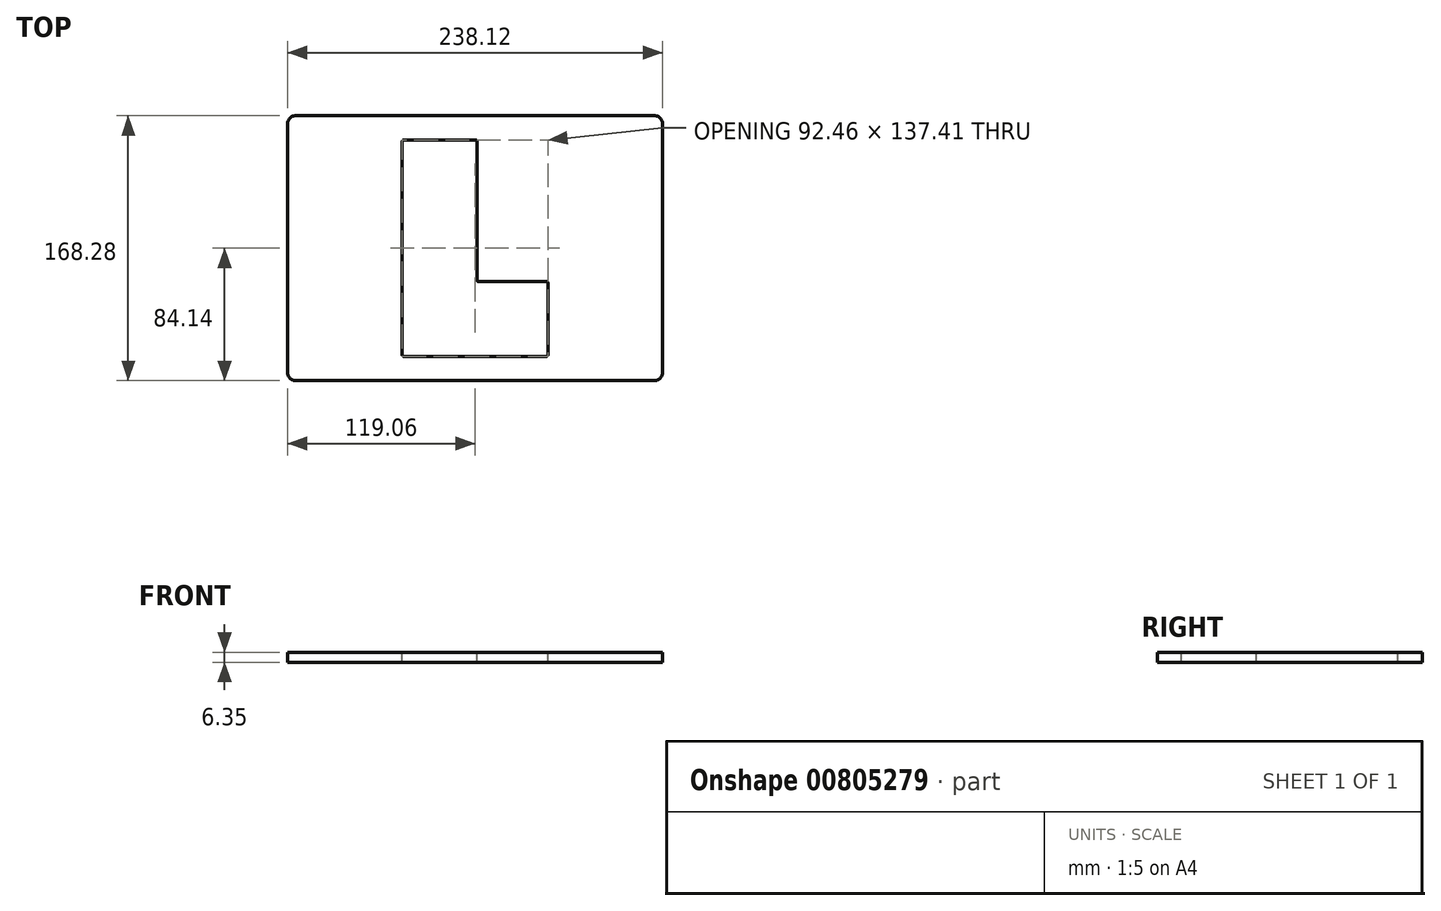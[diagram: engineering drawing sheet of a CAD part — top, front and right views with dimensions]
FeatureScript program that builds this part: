
annotation { "Feature Type Name" : "Feature", "Feature Type Description" : "" }
export const myFeature = defineFeature(function(context is Context, id is Id, definition is map)
    precondition{}
    {
        {
            var Q0;
            Q0=qCreatedBy(makeId("Top.planeOp"),FACE);
            var sketch = newSketch(context, id + "F0", { "sketchPlane" : qUnion([Q0])});
            skLineSegment(sketch, "E0.bottom", {"start": v(-119.06, 84.14) * mm, "end": v(119.06, 84.14) * mm});
            skLineSegment(sketch, "E0.top", {"start": v(-119.06, -84.14) * mm, "end": v(119.06, -84.14) * mm});
            skLineSegment(sketch, "E0.left", {"start": v(-119.06, 84.14) * mm, "end": v(-119.06, -84.14) * mm});
            skLineSegment(sketch, "E0.right", {"start": v(119.06, 84.14) * mm, "end": v(119.06, -84.14) * mm});
            skPoint(sketch, "E0.middle", {"position": v(0, 0) * mm});
            skSolve(sketch);
        }
        {
            var Q0;
            Q0 = qSketchRegion(id + "F0", true);
            extrude(context, id + "F1", {"entities" : qUnion([Q0]), "depth" : 6.35 * mm, "offsetDistance" : 25.4 * mm});
        }
        {
            var Q0;
            Q0=makeQuery(id+"F1.opExtrude","CAP_FACE",FACE,{"disambiguationData":[OSD([sQuery(id+"F0.wireOp",EDGE,"E0.bottom"),sQuery(id+"F0.wireOp",EDGE,"E0.top"),sQuery(id+"F0.wireOp",EDGE,"E0.left"),sQuery(id+"F0.wireOp",EDGE,"E0.right")])],"isStart":false});
            var sketch = newSketch(context, id + "F2", { "sketchPlane" : qUnion([Q0])});
            skLineSegment(sketch, "E1.bottom", {"start": v(0, 67.44) * mm, "end": v(-44.96, 67.44) * mm});
            skLineSegment(sketch, "E1.left", {"start": v(0, 67.44) * mm, "end": v(0, -22.48) * mm});
            skLineSegment(sketch, "E1.right", {"start": v(-44.96, 67.44) * mm, "end": v(-44.96, -67.44) * mm});
            skLineSegment(sketch, "E2.top", {"start": v(0, -22.48) * mm, "end": v(44.96, -22.48) * mm});
            skLineSegment(sketch, "E2.right", {"start": v(44.96, -67.44) * mm, "end": v(44.96, -22.48) * mm});
            skLineSegment(sketch, "E3", {"start": v(-44.96, -67.44) * mm, "end": v(44.96, -67.44) * mm});
            skSolve(sketch);
        }
        {
            var Q0;
            Q0 = qSketchRegion(id + "F2", true);
            extrude(context, id + "F3", {"entities" : qUnion([Q0]), "operationType" : NewBodyOperationType.REMOVE, "oppositeDirection" : true, "depth" : 25.4 * mm, "offsetDistance" : 25.4 * mm});
        }
        {
            var Q0;
            Q0 = qSketchRegion(id + "F2", true);
            extrude(context, id + "F4", {"entities" : qUnion([Q0]), "operationType" : NewBodyOperationType.REMOVE, "endBound" : BoundingType.THROUGH_ALL, "oppositeDirection" : true, "depth" : 25.4 * mm, "offsetDistance" : 25.4 * mm});
        }
        {
            var Q0;
            Q0=makeQuery(id+"F1.opExtrude","CAP_FACE",FACE,{"disambiguationData":[OSD([sQuery(id+"F0.wireOp",EDGE,"E0.bottom"),sQuery(id+"F0.wireOp",EDGE,"E0.top"),sQuery(id+"F0.wireOp",EDGE,"E0.left"),sQuery(id+"F0.wireOp",EDGE,"E0.right")])],"isStart":false});
            var sketch = newSketch(context, id + "F5", { "sketchPlane" : qUnion([Q0])});
            skLineSegment(sketch, "E4.0", {"start": v(1.27, 67.92) * mm, "end": v(1.27, -20.42) * mm});
            skLineSegment(sketch, "E4.1", {"start": v(-46.23, 67.92) * mm, "end": v(-46.23, -67.92) * mm});
            skLineSegment(sketch, "E4.2", {"start": v(-45.44, -68.7) * mm, "end": v(45.44, -68.7) * mm});
            skLineSegment(sketch, "E4.3", {"start": v(0.48, 68.7) * mm, "end": v(-45.44, 68.7) * mm});
            skLineSegment(sketch, "E4.4", {"start": v(46.23, -67.92) * mm, "end": v(46.23, -22) * mm});
            skLineSegment(sketch, "E4.5", {"start": v(2.06, -21.2) * mm, "end": v(45.44, -21.2) * mm});
            skPoint(sketch, "E5.visualSharp", {"position": v(-46.23, 68.7) * mm});
            skArc(sketch, "E5.filletArc", {"start": v(-45.44, 68.7) * mm, "mid": v(-46, 68.48) * mm, "end": v(-46.23, 67.92) * mm});
            skPoint(sketch, "E6.visualSharp", {"position": v(1.27, 68.7) * mm});
            skArc(sketch, "E6.filletArc", {"start": v(1.27, 67.92) * mm, "mid": v(1.04, 68.48) * mm, "end": v(0.48, 68.7) * mm});
            skPoint(sketch, "E7.visualSharp", {"position": v(1.27, -21.2) * mm});
            skArc(sketch, "E7.filletArc", {"start": v(1.27, -20.42) * mm, "mid": v(1.5, -20.98) * mm, "end": v(2.06, -21.2) * mm});
            skPoint(sketch, "E8.visualSharp", {"position": v(46.23, -21.2) * mm});
            skArc(sketch, "E8.filletArc", {"start": v(46.23, -22) * mm, "mid": v(46, -21.44) * mm, "end": v(45.44, -21.2) * mm});
            skPoint(sketch, "E9.visualSharp", {"position": v(46.23, -68.7) * mm});
            skArc(sketch, "E9.filletArc", {"start": v(45.44, -68.7) * mm, "mid": v(46, -68.48) * mm, "end": v(46.23, -67.92) * mm});
            skPoint(sketch, "E10.visualSharp", {"position": v(-46.23, -68.7) * mm});
            skArc(sketch, "E10.filletArc", {"start": v(-46.23, -67.92) * mm, "mid": v(-46, -68.48) * mm, "end": v(-45.44, -68.7) * mm});
            skSolve(sketch);
        }
        {
            var Q0;
            Q0 = qSketchRegion(id + "F5", true);
            extrude(context, id + "F6", {"entities" : qUnion([Q0]), "operationType" : NewBodyOperationType.REMOVE, "endBound" : BoundingType.THROUGH_ALL, "oppositeDirection" : true, "depth" : 25.4 * mm, "offsetDistance" : 25.4 * mm});
        }
        {
            var Q0;
            Q0=makeQuery(id+"F1.opExtrude","SWEPT_EDGE",EDGE,{"disambiguationData":[OSD([sQuery(id+"F0.wireOp",EDGE,"E0.top"),sQuery(id+"F0.wireOp",EDGE,"E0.left")])]});
            var Q1;
            Q1=makeQuery(id+"F1.opExtrude","SWEPT_EDGE",EDGE,{"disambiguationData":[OSD([sQuery(id+"F0.wireOp",EDGE,"E0.bottom"),sQuery(id+"F0.wireOp",EDGE,"E0.left")])]});
            var Q2;
            Q2=makeQuery(id+"F1.opExtrude","SWEPT_EDGE",EDGE,{"disambiguationData":[OSD([sQuery(id+"F0.wireOp",EDGE,"E0.top"),sQuery(id+"F0.wireOp",EDGE,"E0.right")])]});
            var Q3;
            Q3=makeQuery(id+"F1.opExtrude","SWEPT_EDGE",EDGE,{"disambiguationData":[OSD([sQuery(id+"F0.wireOp",EDGE,"E0.bottom"),sQuery(id+"F0.wireOp",EDGE,"E0.right")])]});
            fillet(context, id + "F7", {"entities" : qUnion([Q0, Q1, Q2, Q3]), "radius" : 5.08 * mm, "tangentPropagation" : true, "allowEdgeOverflow" : false});
        }
    });
